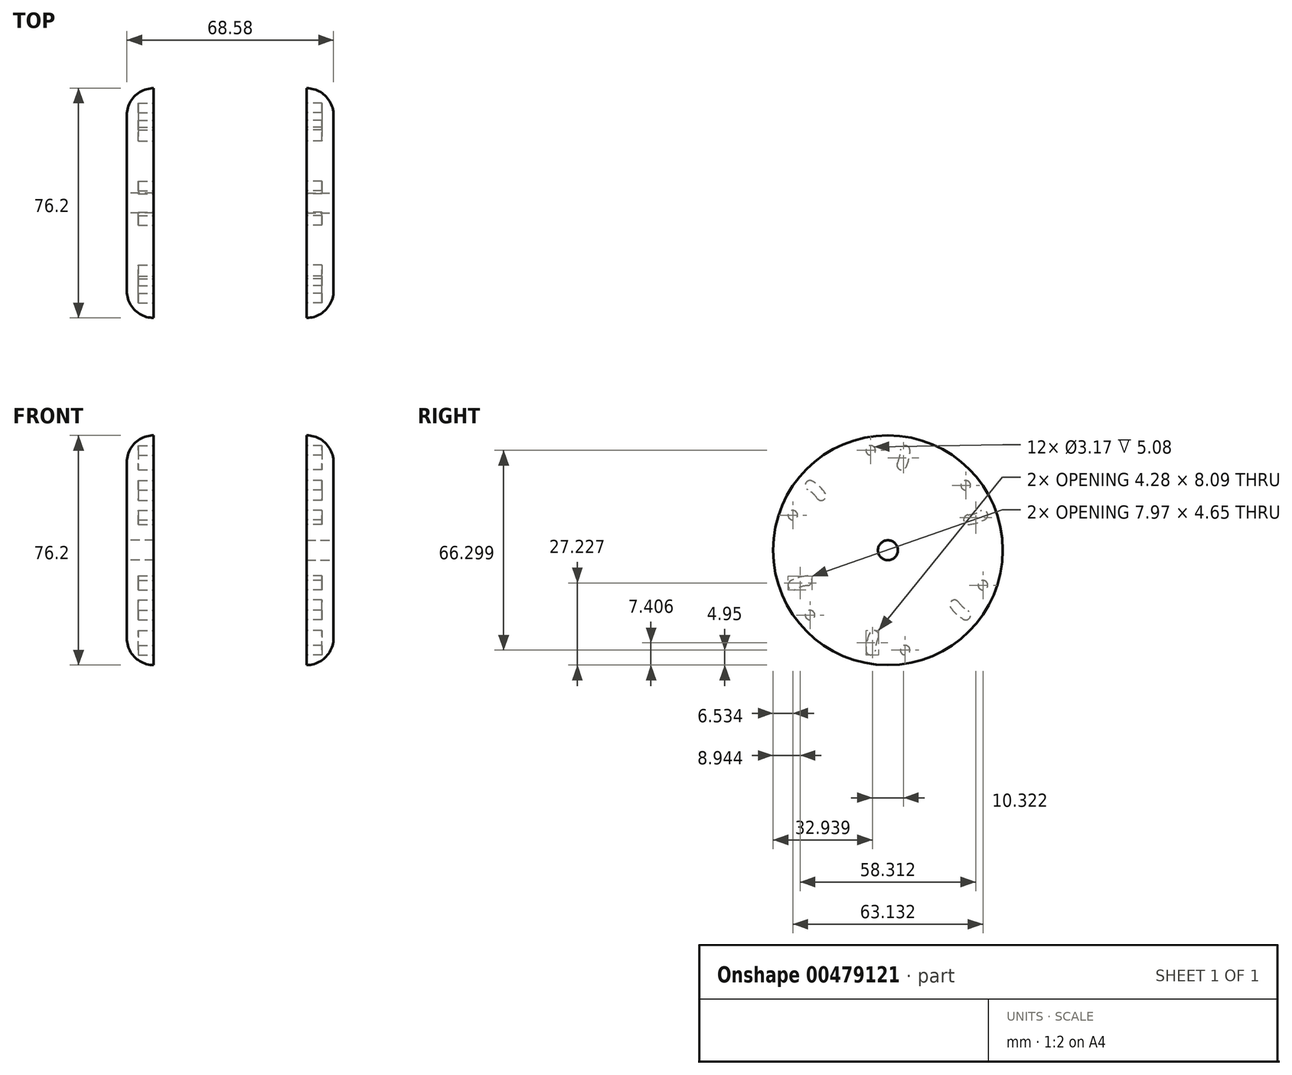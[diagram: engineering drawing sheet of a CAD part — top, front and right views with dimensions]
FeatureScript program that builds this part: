
annotation { "Feature Type Name" : "Feature", "Feature Type Description" : "" }
export const myFeature = defineFeature(function(context is Context, id is Id, definition is map)
    precondition{}
    {
        {
            var Q0;
            Q0=qCreatedBy(makeId("Right.planeOp"),FACE);
            var sketch = newSketch(context, id + "F0", { "sketchPlane" : qUnion([Q0])});
            skCircle(sketch, "E0", {"center": v(0, 0) * mm, "radius": 38.1 * mm});
            skSolve(sketch);
        }
        {
            var Q0;
            Q0 = qSketchRegion(id + "F0", true);
            extrude(context, id + "F1", {"entities" : qUnion([Q0]), "depth" : 8.9 * mm});
        }
        {
            var Q0;
            Q0=makeQuery(id+"F1.opExtrude","CAP_EDGE",EDGE,{"disambiguationData":[OSD([sQuery(id+"F0.wireOp",EDGE,"E0")])],"isStart":false});
            fillet(context, id + "F2", {"entities" : qUnion([Q0]), "radius" : 8.9 * mm, "tangentPropagation" : true, "allowEdgeOverflow" : false});
        }
        {
            var Q0;
            Q0=makeQuery(id+"F1.opExtrude","CAP_FACE",FACE,{"disambiguationData":[OSD([sQuery(id+"F0.wireOp",EDGE,"E0")])],"isStart":false});
            var sketch = newSketch(context, id + "F3", { "sketchPlane" : qUnion([Q0])});
            skCircle(sketch, "E1", {"center": v(0, 0) * mm, "radius": 3.3 * mm});
            skSolve(sketch);
        }
        {
            var Q0;
            Q0=makeQuery(id+"F3.imprint","IMPRINT",FACE,{"disambiguationData":[TD([[makeQuery(id+"F3.imprint","IMPRINT",EDGE,{"derivedFrom":sQuery(id+"F3.wireOp",EDGE,"E1")}),1.0]])]});
            extrude(context, id + "F4", {"entities" : qUnion([Q0]), "operationType" : NewBodyOperationType.REMOVE, "oppositeDirection" : true, "depth" : 8.9 * mm});
        }
        {
            var Q0;
            Q0=makeQuery(id+"F1.opExtrude","CAP_FACE",FACE,{"disambiguationData":[OSD([sQuery(id+"F0.wireOp",EDGE,"E0")])],"isStart":true});
            var sketch = newSketch(context, id + "F5", { "sketchPlane" : qUnion([Q0])});
            skCircle(sketch, "E2", {"center": v(5.72, 33.15) * mm, "radius": 1.59 * mm});
            skCircle(sketch, "E3", {"center": v(-5.72, 33.15) * mm, "radius": 1.59 * mm});
            skArc(sketch, "E4", {"start": v(-5.72, 33.15) * mm, "mid": v(-5.43, 30.63) * mm, "end": v(-4.6, 28.24) * mm});
            skCircle(sketch, "E5", {"center": v(-4.6, 28.24) * mm, "radius": 1.59 * mm});
            skArc(sketch, "E6", {"start": v(-4.13, 33.15) * mm, "mid": v(-3.89, 30.98) * mm, "end": v(-3.17, 28.92) * mm});
            skArc(sketch, "E7", {"start": v(-7.3, 33.15) * mm, "mid": v(-6.98, 30.28) * mm, "end": v(-6.04, 27.55) * mm});
            skArc(sketch, "E8.1.0", {"start": v(-30.77, 13) * mm, "mid": v(-28.77, 12.13) * mm, "end": v(-26.63, 11.71) * mm});
            skCircle(sketch, "E8.1.1", {"center": v(-31.57, 11.63) * mm, "radius": 1.59 * mm});
            skArc(sketch, "E8.1.2", {"start": v(-32.36, 10.25) * mm, "mid": v(-29.71, 9.1) * mm, "end": v(-26.88, 8.55) * mm});
            skCircle(sketch, "E8.1.3", {"center": v(-26.75, 10.13) * mm, "radius": 1.59 * mm});
            skCircle(sketch, "E8.1.4", {"center": v(-25.85, 21.52) * mm, "radius": 1.59 * mm});
            skArc(sketch, "E8.2.0", {"start": v(-26.64, -20.15) * mm, "mid": v(-24.89, -18.86) * mm, "end": v(-23.46, -17.2) * mm});
            skCircle(sketch, "E8.2.1", {"center": v(-25.85, -21.52) * mm, "radius": 1.59 * mm});
            skArc(sketch, "E8.2.2", {"start": v(-25.06, -22.9) * mm, "mid": v(-22.73, -21.19) * mm, "end": v(-20.84, -19) * mm});
            skCircle(sketch, "E8.2.3", {"center": v(-22.15, -18.1) * mm, "radius": 1.59 * mm});
            skCircle(sketch, "E8.2.4", {"center": v(-31.57, -11.63) * mm, "radius": 1.59 * mm});
            skArc(sketch, "E8.3.0", {"start": v(4.13, -33.15) * mm, "mid": v(3.89, -30.98) * mm, "end": v(3.17, -28.92) * mm});
            skCircle(sketch, "E8.3.1", {"center": v(5.71, -33.15) * mm, "radius": 1.59 * mm});
            skArc(sketch, "E8.3.2", {"start": v(7.3, -33.15) * mm, "mid": v(6.98, -30.28) * mm, "end": v(6.04, -27.55) * mm});
            skCircle(sketch, "E8.3.3", {"center": v(4.6, -28.24) * mm, "radius": 1.59 * mm});
            skCircle(sketch, "E8.3.4", {"center": v(-5.72, -33.15) * mm, "radius": 1.59 * mm});
            skArc(sketch, "E8.4.0", {"start": v(30.77, -13) * mm, "mid": v(28.77, -12.13) * mm, "end": v(26.63, -11.71) * mm});
            skCircle(sketch, "E8.4.1", {"center": v(31.57, -11.63) * mm, "radius": 1.59 * mm});
            skArc(sketch, "E8.4.2", {"start": v(32.36, -10.25) * mm, "mid": v(29.71, -9.1) * mm, "end": v(26.88, -8.55) * mm});
            skCircle(sketch, "E8.4.3", {"center": v(26.75, -10.13) * mm, "radius": 1.59 * mm});
            skCircle(sketch, "E8.4.4", {"center": v(25.85, -21.52) * mm, "radius": 1.59 * mm});
            skArc(sketch, "E8.5.0", {"start": v(26.64, 20.15) * mm, "mid": v(24.89, 18.86) * mm, "end": v(23.46, 17.2) * mm});
            skCircle(sketch, "E8.5.1", {"center": v(25.85, 21.52) * mm, "radius": 1.59 * mm});
            skArc(sketch, "E8.5.2", {"start": v(25.06, 22.9) * mm, "mid": v(22.73, 21.19) * mm, "end": v(20.84, 19) * mm});
            skCircle(sketch, "E8.5.3", {"center": v(22.15, 18.1) * mm, "radius": 1.59 * mm});
            skCircle(sketch, "E8.5.4", {"center": v(31.57, 11.63) * mm, "radius": 1.59 * mm});
            skPoint(sketch, "E8.center", {"position": v(0, 0) * mm});
            skSolve(sketch);
        }
        {
            var Q0;
            Q0 = qSketchRegion(id + "F5", true);
            extrude(context, id + "F6", {"entities" : qUnion([Q0]), "operationType" : NewBodyOperationType.REMOVE, "oppositeDirection" : true, "depth" : 5.08 * mm});
        }
        {
            var Q0;
            Q0=qCreatedBy(makeId("Right.planeOp"),FACE);
            cPlane(context, id + "F7", {"entities" : qUnion([Q0]), "cplaneType" : CPlaneType.OFFSET, "offset" : 25.4 * mm, "oppositeDirection" : true, "width" : 152.4 * mm, "height" : 152.4 * mm});
        }
        {
            var Q0;
            Q0=makeQuery(id+"F1.opExtrude","SWEPT_BODY",BODY,{"disambiguationData":[OSD([sQuery(id+"F0.wireOp",EDGE,"E0")])]});
            var Q1;
            Q1=qCreatedBy(id+"F7.planeOp",FACE);
            mirror(context, id + "F8", {"entities" : qUnion([Q0]), "mirrorPlane" : qUnion([Q1])});
        }
    });
